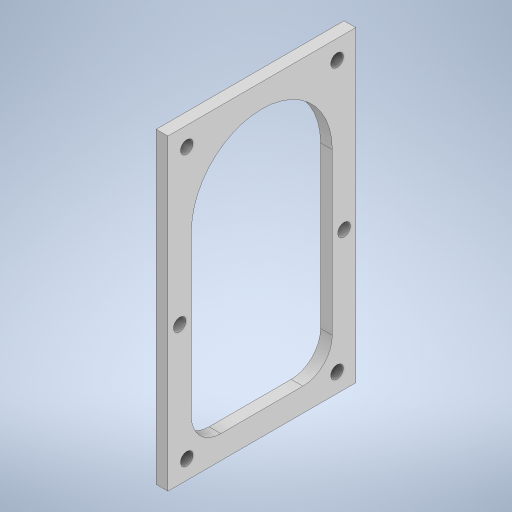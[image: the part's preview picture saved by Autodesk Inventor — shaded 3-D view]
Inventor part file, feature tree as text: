
AUTODESK INVENTOR PART (.ipt)
format: ipt  version: 2023 (Build 270158000, 158)  size: 277,504 bytes
history: native  units: in
note: dims shown in document units (in); Inventor stores cm internally (conversion verified against a paired STEP export)
features: extrude x1
ambient origin geometry x8: Origin, YZ Plane, XZ Plane, XY Plane, X Axis, Y Axis, Z Axis, Center Point
bodies: Solid1 (feature_tree)
feature tree (1):
  extrude  "Extrusion1"  Depth=3.275in
